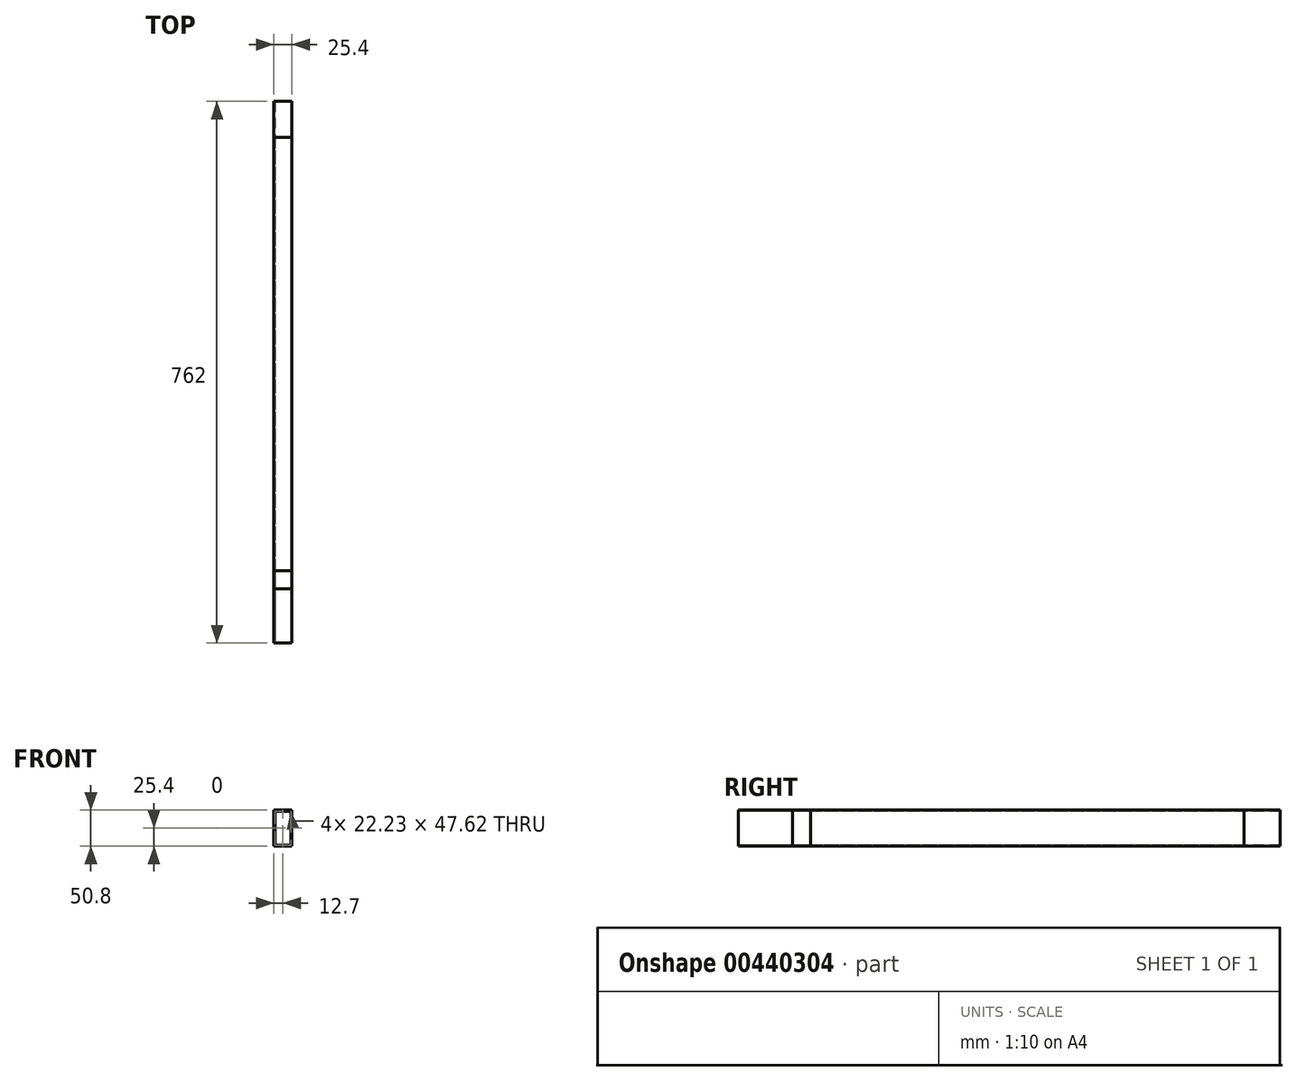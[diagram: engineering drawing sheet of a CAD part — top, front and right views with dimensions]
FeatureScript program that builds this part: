
annotation { "Feature Type Name" : "Feature", "Feature Type Description" : "" }
export const myFeature = defineFeature(function(context is Context, id is Id, definition is map)
    precondition{}
    {
        {
            assignVariable(context, id + "F0", {"name" : "robot_depth", "anyValue" : 762 * mm});
        }
        {
            assignVariable(context, id + "F1", {"name" : "robot_width", "anyValue" : 863.6 * mm});
        }
        {
            assignVariable(context, id + "F2", {"name" : "body_tube_width", "anyValue" : 25.4 * mm});
        }
        {
            assignVariable(context, id + "F3", {"name" : "body_tube_height", "anyValue" : 50.8 * mm});
        }
        {
            var Q0;
            Q0=qCreatedBy(makeId("Front.planeOp"),FACE);
            var sketch = newSketch(context, id + "F4", { "sketchPlane" : qUnion([Q0])});
            skLineSegment(sketch, "E0.bottom", {"start": v(0, 0) * mm, "end": v(25.4, 0) * mm});
            skLineSegment(sketch, "E0.top", {"start": v(0, 50.8) * mm, "end": v(25.4, 50.8) * mm});
            skLineSegment(sketch, "E0.left", {"start": v(0, 0) * mm, "end": v(0, 50.8) * mm});
            skLineSegment(sketch, "E0.right", {"start": v(25.4, 0) * mm, "end": v(25.4, 50.8) * mm});
            skLineSegment(sketch, "E1.bottom", {"start": v(1.59, 1.59) * mm, "end": v(23.81, 1.59) * mm});
            skLineSegment(sketch, "E1.top", {"start": v(1.59, 49.21) * mm, "end": v(23.81, 49.21) * mm});
            skLineSegment(sketch, "E1.left", {"start": v(1.59, 1.59) * mm, "end": v(1.59, 49.21) * mm});
            skLineSegment(sketch, "E1.right", {"start": v(23.81, 1.59) * mm, "end": v(23.81, 49.21) * mm});
            skLineSegment(sketch, "E2", {"start": v(1.59, 1.59) * mm, "end": v(1.59, 0) * mm, "construction": true});
            skLineSegment(sketch, "E3", {"start": v(1.59, 1.59) * mm, "end": v(0, 1.59) * mm, "construction": true});
            skLineSegment(sketch, "E4", {"start": v(23.81, 49.21) * mm, "end": v(23.81, 50.8) * mm, "construction": true});
            skLineSegment(sketch, "E5", {"start": v(23.81, 49.21) * mm, "end": v(25.4, 49.21) * mm, "construction": true});
            skSolve(sketch);
        }
        {
            var Q0;
            Q0 = qSketchRegion(id + "F4", true);
            extrude(context, id + "F5", {"entities" : qUnion([Q0]), "oppositeDirection" : true, "depth" : getVariable(context, 'robot_depth')});
        }
        {
            var Q0;
            Q0 = qSketchRegion(id + "F4", true);
            extrude(context, id + "F6", {"entities" : qUnion([Q0]), "oppositeDirection" : true, "depth" : getVariable(context, 'robot_width') - 2 * getVariable(context, 'body_tube_width') - 2 * getVariable(context, 'body_tube_height')});
        }
        {
            var Q0;
            Q0 = qSketchRegion(id + "F4", true);
            extrude(context, id + "F7", {"entities" : qUnion([Q0]), "oppositeDirection" : true, "depth" : 152.4 * mm - getVariable(context, 'body_tube_width') - getVariable(context, 'body_tube_height')});
        }
        {
            var Q0;
            Q0 = qSketchRegion(id + "F4", true);
            extrude(context, id + "F8", {"entities" : qUnion([Q0]), "oppositeDirection" : true, "depth" : 101.6 * mm});
        }
    });
